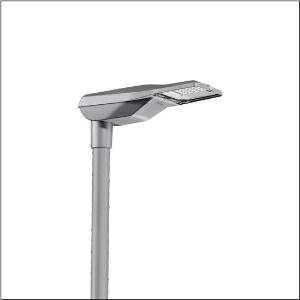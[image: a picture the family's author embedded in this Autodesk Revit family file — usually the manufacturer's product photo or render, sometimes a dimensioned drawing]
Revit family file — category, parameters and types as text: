
# Revit family: streetlight_sl_21_iq_micro___st0_8a_5xe1c41g08cb_fbf2
name_source: partatom
category: Lighting Fixtures
units: mm (PartAtom-declared; Revit-internal decimal feet)

## family parameters
Cut with Voids When Loaded = No
Host = Face
Light Source = No
Part Type = Normal
Room Calculation Point = No
Round Connector Dimension = Use Diameter
Shared = No

## types (1)
- --- (1 x LED, 2980 lm, 19.4 W, 4000K)
    Apparent Load = 19 VA
    CIE Flux Codes = 38 75 97 100 100
    Color Rendering = 70
    Color Temperature = 4000K
    Default Elevation = 1800 mm
    Description = Streetlight SL 21 iQ micro, mast luminaire, primary light control with lens, of PMMA, primary optical cover: cover, of toughened safety glass, transparent, light distribution: ST0.8a, light emission: direct distribution, primary light characteristic: asymmetric, installation type: post-top, side-entry, LED, High Power LED, rated luminous flux: 2.980lm, luminous efficacy: 154lm/W, light colour: 740, colour temperature: 4000K, control: Street-Remote, Auto-Match, Temp-Guard, Lumen-Switch, Night-Set, Smart-Wire, Light-Fading, Desk-Remote (wireless, voltage-free reading and setting of iQ features in the workshop via application-optimized NFC function/RFID function), optimised constant luminous flux control (CLO 2.0), presetting dimming linear, mains connection: 220..240V, AC, 50/60Hz, start of lifetime: 19W, end of service life: 20W, reduction: 10W, luminaire housing, of diecast aluminium, powder-coated, Siteco® metallic grey (DB 702S), corrosivity category C5 mid according to DIN EN ISO 12944, please order mast flange separately, inclination adjustable: 0°, 5°, 10°, 15°, sealing non-destructively replaceable, multi-level sealing system, length: 528mm, width: 235mm, height: 110mm, mast flange for spigot size: 42mm (side-entry): 5XC10008XM4, 60/48mm (side-entry/post-top): 5XC10108XM2, 76/60mm (side-entry/post-top): 5XC10108XM1, protection rating (complete): IP66, insulation class (complete): insulation class II (safety insulation), certification: CE, ENEC, ENEC+, VDE, impact resistance: IK09, permissible operating ambient temperature for outdoor applications: -40..+50°C, standard-compliant lighting for roads and squares, packaging unit: 1 piece

Light Distribution: ST0.8a
    Height = 110 mm
    Lamp = 1 x LED
    Lamp Light Flux = 2980 lm
    Lamp Power = 19.4 W
    Lamp count = 1
    Length = 528 mm
    Luminous efficacy = 154 lm/W
    Manufacturer = Siteco
    ModVariant = No
    Model = 5XE1C41G08CB
    Number of Poles = 1
    OnlyDefault = Yes
    Power Factor = 1
    Product Name = Streetlight SL 21 iQ micro | ST0.8a
    Product group = mast luminaire | pylon top
    ProductGroupID = 6100
    Protection Class = Protection class II
    Protection Degree = IP 66
    RLX_Detail_Level = 1
    RLX_Emergency_Light_Flux = 0 lm
    RLX_Emergency_Type = 0
    RLX_Emergency_Type_DB = No
    RlxData = <blob elided: 98665 chars, md5=3d4572e6>
    Socket = socket
    Standby Power = 0 W
    System Light Flux = 2980 lm
    System Power = 19 W
    Type Comments = factory setting: luminous flux: 100 % | dim-lin: 254 | 387 mA
    Type Image = l_1006881.jpg
    URL = http://relux.com
    VarID = @adj_069681
    Voltage = 0 V
    Weight = 0.00 kg
    Width = 235 mm

## geometry (parser evidence)
native form markers: Blend x4, Sweep x11
no freeform markers — native parametric forms only
